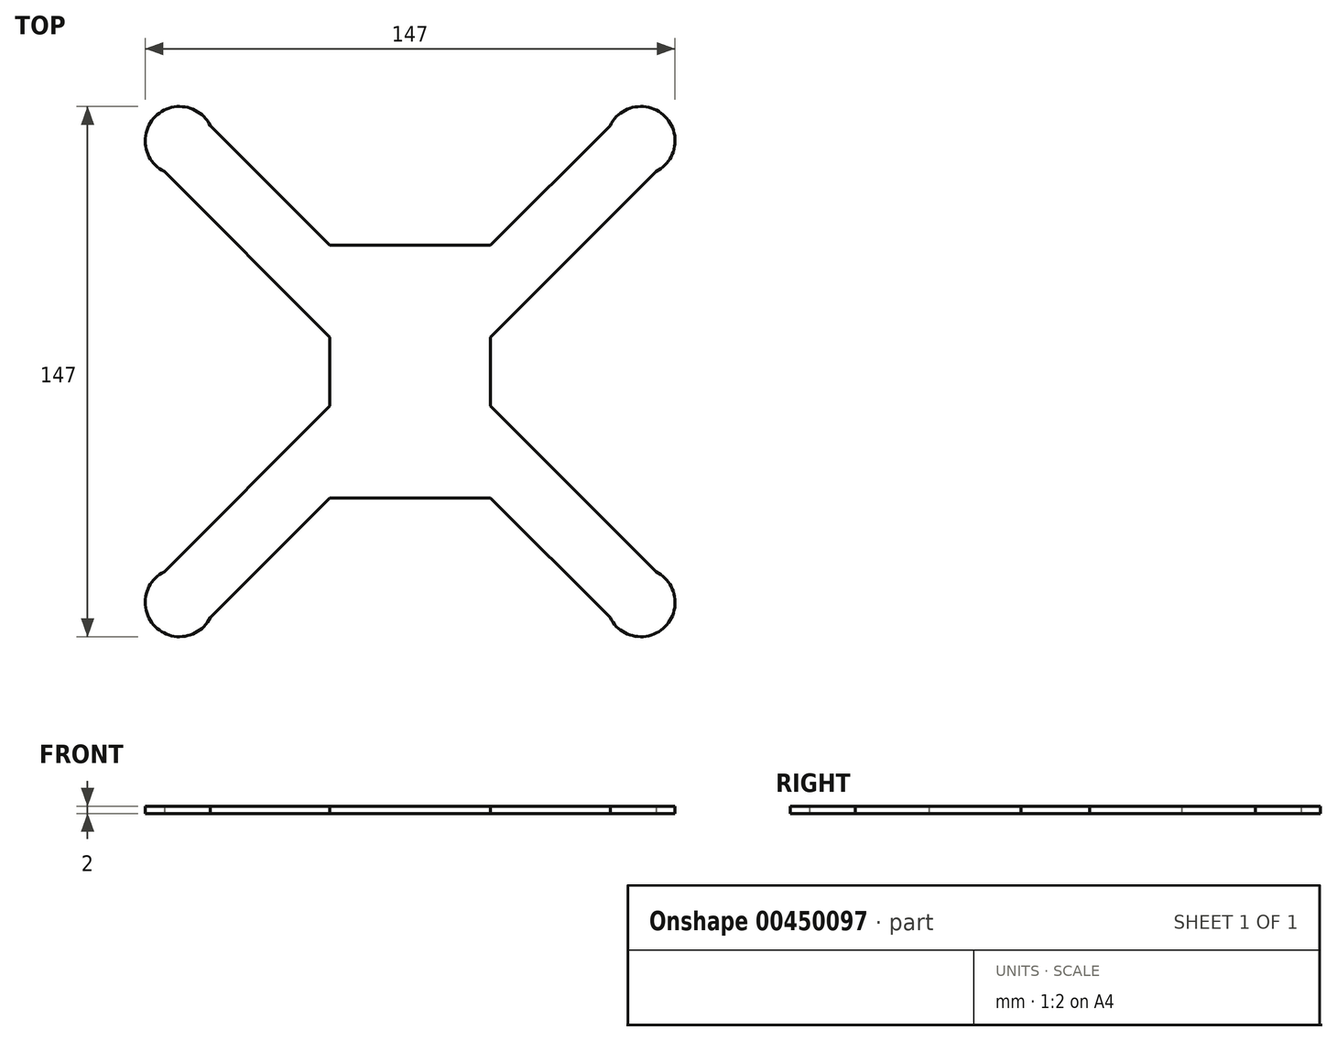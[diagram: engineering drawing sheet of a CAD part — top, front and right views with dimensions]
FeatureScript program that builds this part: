
annotation { "Feature Type Name" : "Feature", "Feature Type Description" : "" }
export const myFeature = defineFeature(function(context is Context, id is Id, definition is map)
    precondition{}
    {
        {
            var Q0;
            Q0=qCreatedBy(makeId("Top.planeOp"),FACE);
            var sketch = newSketch(context, id + "F0", { "sketchPlane" : qUnion([Q0])});
            skLineSegment(sketch, "E0", {"start": v(0, 0) * mm, "end": v(-64, 64) * mm, "construction": true});
            skArc(sketch, "E1", {"start": v(-55.49, 68.21) * mm, "mid": v(-70.72, 70.72) * mm, "end": v(-68.21, 55.49) * mm});
            skLineSegment(sketch, "E2.0", {"start": v(-22.27, 35) * mm, "end": v(-55.49, 68.21) * mm});
            skLineSegment(sketch, "E3.0", {"start": v(-22.27, 9.54) * mm, "end": v(-68.21, 55.49) * mm});
            skLineSegment(sketch, "E4.MirrorCS", {"start": v(22.27, 35) * mm, "end": v(55.49, 68.21) * mm});
            skArc(sketch, "E5.MirrorCS", {"start": v(55.49, 68.21) * mm, "mid": v(70.72, 70.72) * mm, "end": v(68.21, 55.49) * mm});
            skLineSegment(sketch, "E6.MirrorCS", {"start": v(22.27, 9.54) * mm, "end": v(68.21, 55.49) * mm});
            skLineSegment(sketch, "E7", {"start": v(22.27, 35) * mm, "end": v(-22.27, 35) * mm});
            skPoint(sketch, "E8.orphan", {"position": v(0, 12.73) * mm});
            skLineSegment(sketch, "E9", {"start": v(-22.27, 9.54) * mm, "end": v(-22.27, 0) * mm});
            skPoint(sketch, "E10.orphan", {"position": v(-12.73, 0) * mm});
            skLineSegment(sketch, "E11", {"start": v(22.27, 9.54) * mm, "end": v(22.27, 0) * mm});
            skPoint(sketch, "E12.orphan", {"position": v(12.73, 0) * mm});
            skLineSegment(sketch, "E13.MirrorCS", {"start": v(22.27, -35) * mm, "end": v(-22.27, -35) * mm});
            skLineSegment(sketch, "E14.MirrorCS", {"start": v(22.27, -35) * mm, "end": v(55.49, -68.21) * mm});
            skLineSegment(sketch, "E15.MirrorCS", {"start": v(-22.27, -35) * mm, "end": v(-55.49, -68.21) * mm});
            skArc(sketch, "E16.MirrorCS", {"start": v(-55.49, -68.21) * mm, "mid": v(-70.72, -70.72) * mm, "end": v(-68.21, -55.49) * mm});
            skArc(sketch, "E17.MirrorCS", {"start": v(55.49, -68.21) * mm, "mid": v(70.72, -70.72) * mm, "end": v(68.21, -55.49) * mm});
            skLineSegment(sketch, "E18.MirrorCS", {"start": v(-22.27, -9.54) * mm, "end": v(-68.21, -55.49) * mm});
            skLineSegment(sketch, "E19.MirrorCS", {"start": v(22.27, -9.54) * mm, "end": v(68.21, -55.49) * mm});
            skLineSegment(sketch, "E20.MirrorCS", {"start": v(22.27, -9.54) * mm, "end": v(22.27, 0) * mm});
            skLineSegment(sketch, "E21.MirrorCS", {"start": v(-22.27, -9.54) * mm, "end": v(-22.27, 0) * mm});
            skSolve(sketch);
        }
        {
            var Q0;
            Q0 = qSketchRegion(id + "F0", true);
            extrude(context, id + "F1", {"entities" : qUnion([Q0]), "depth" : 2 * mm});
        }
    });
